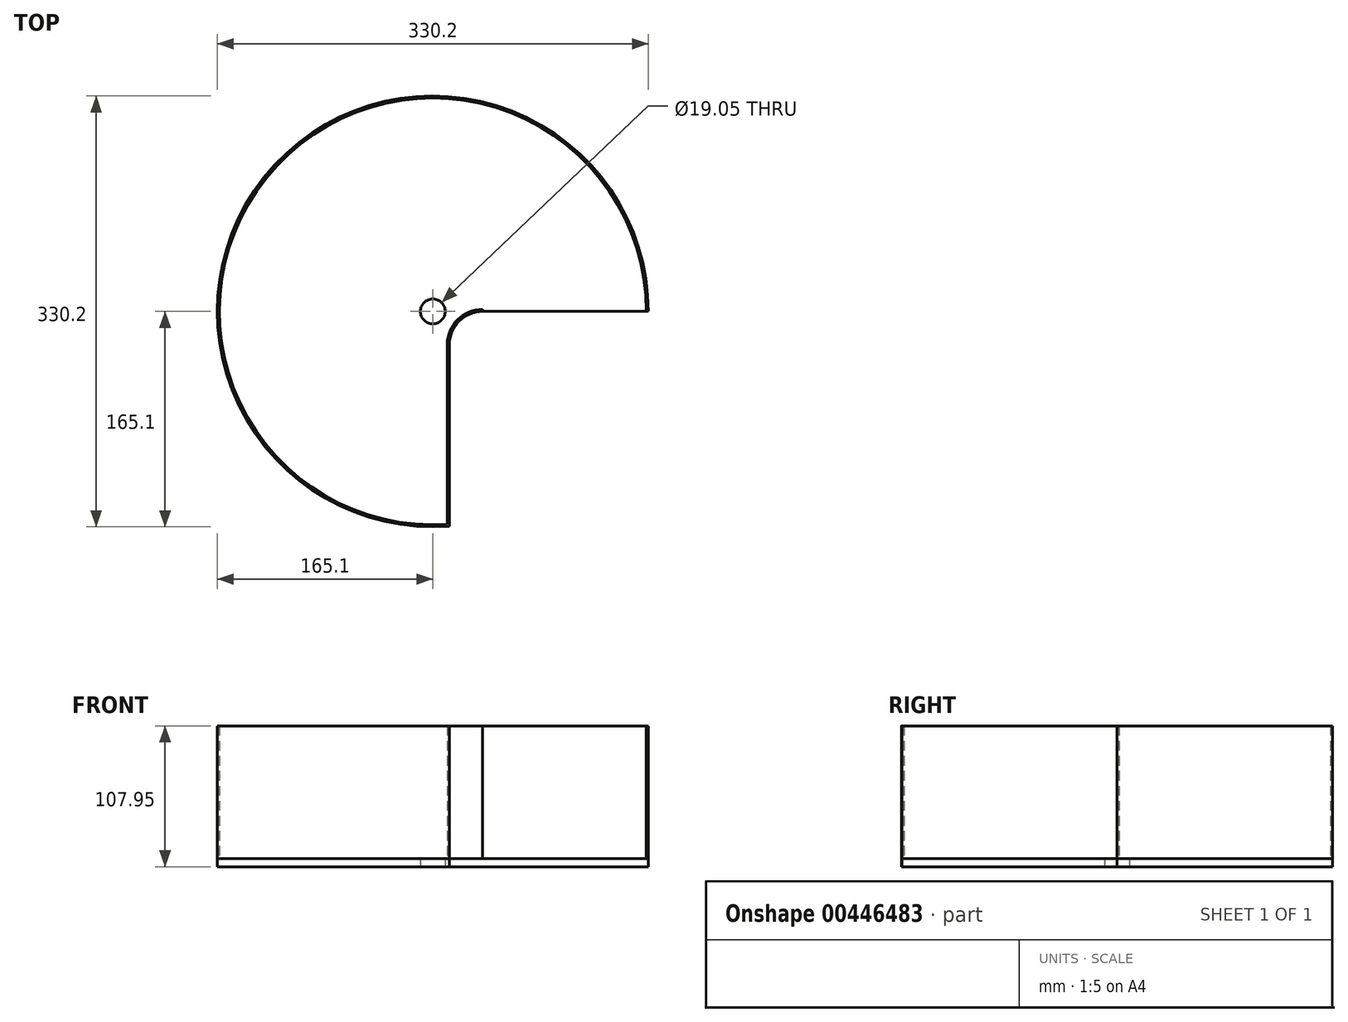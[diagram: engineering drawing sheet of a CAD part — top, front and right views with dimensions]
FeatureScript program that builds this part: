
annotation { "Feature Type Name" : "Feature", "Feature Type Description" : "" }
export const myFeature = defineFeature(function(context is Context, id is Id, definition is map)
    precondition{}
    {
        {
            var Q0;
            Q0=qCreatedBy(makeId("Top.planeOp"),FACE);
            var sketch = newSketch(context, id + "F0", { "sketchPlane" : qUnion([Q0])});
            skArc(sketch, "E0", {"start": v(165.1, 0) * mm, "mid": v(-121.15, 112.16) * mm, "end": v(12.7, -164.61) * mm});
            skLineSegment(sketch, "E1", {"start": v(165.1, 0) * mm, "end": v(38.1, 0) * mm});
            skLineSegment(sketch, "E2", {"start": v(12.7, -25.4) * mm, "end": v(12.7, -164.61) * mm});
            skPoint(sketch, "E3.visualSharp", {"position": v(12.7, 0) * mm});
            skArc(sketch, "E3.filletArc", {"start": v(38.1, 0) * mm, "mid": v(20.14, -7.44) * mm, "end": v(12.7, -25.4) * mm});
            skSolve(sketch);
        }
        {
            var Q0;
            Q0 = qSketchRegion(id + "F0", true);
            extrude(context, id + "F1", {"entities" : qUnion([Q0]), "depth" : 6.35 * mm});
        }
        {
            var Q0;
            Q0=makeQuery(id+"F1.opExtrude","CAP_FACE",FACE,{"disambiguationData":[OSD([sQuery(id+"F0.wireOp",EDGE,"E0"),sQuery(id+"F0.wireOp",EDGE,"E1"),sQuery(id+"F0.wireOp",EDGE,"E2"),sQuery(id+"F0.wireOp",EDGE,"E3.filletArc")])],"isStart":false});
            var sketch = newSketch(context, id + "F2", { "sketchPlane" : qUnion([Q0])});
            skArc(sketch, "E4.0", {"start": v(38.1, 1.59) * mm, "mid": v(19.02, -6.32) * mm, "end": v(11.11, -25.4) * mm});
            skLineSegment(sketch, "E4.1", {"start": v(11.11, -25.4) * mm, "end": v(11.11, -163.13) * mm});
            skArc(sketch, "E4.2", {"start": v(163.51, 0) * mm, "mid": v(-119.49, 111.62) * mm, "end": v(11.11, -163.13) * mm});
            skLineSegment(sketch, "E5", {"start": v(38.1, 1.59) * mm, "end": v(38.1, 0) * mm});
            skLineSegment(sketch, "E6", {"start": v(163.51, 0) * mm, "end": v(165.1, 0) * mm});
            skSolve(sketch);
        }
        {
            var Q0;
            Q0 = qSketchRegion(id + "F2", true);
            var Q1;
            Q1=makeQuery(id+"F2.imprint","IMPRINT",FACE,{"disambiguationData":[TD([[makeQuery(id+"F2.imprint","IMPRINT",EDGE,{"derivedFrom":sQuery(id+"F2.wireOp",EDGE,"E4.0")}),1.0]])]});
            extrude(context, id + "F3", {"entities" : qUnion([Q0, Q1]), "depth" : 101.6 * mm});
        }
        {
            var Q0;
            Q0=makeQuery(id+"F1.opExtrude","CAP_FACE",FACE,{"disambiguationData":[OSD([sQuery(id+"F0.wireOp",EDGE,"E0"),sQuery(id+"F0.wireOp",EDGE,"E1"),sQuery(id+"F0.wireOp",EDGE,"E2"),sQuery(id+"F0.wireOp",EDGE,"E3.filletArc")])],"isStart":false});
            var sketch = newSketch(context, id + "F4", { "sketchPlane" : qUnion([Q0])});
            skPoint(sketch, "E7", {"position": v(0, 0) * mm});
            skSolve(sketch);
        }
        {
            var Q0;
            Q0=sQuery(id+"F4.wireOp",VERTEX,"E7");
            var Q1;
            Q1=makeQuery(id+"F1.opExtrude","SWEPT_BODY",BODY,{"disambiguationData":[OSD([sQuery(id+"F0.wireOp",EDGE,"E0"),sQuery(id+"F0.wireOp",EDGE,"E1"),sQuery(id+"F0.wireOp",EDGE,"E2"),sQuery(id+"F0.wireOp",EDGE,"E3.filletArc")])]});
            hole(context, id + "F5", {"style" : HoleStyle.SIMPLE, "endStyle" : HoleEndStyle.THROUGH, "holeDiameter" : 19.05 * mm, "isTappedThrough" : true, "tappedDepth" : 12.7 * mm, "tapClearance" : 3, "locations" : qUnion([Q0]), "scope" : qUnion([Q1]), "startStyle" : HoleStartStyle.PART});
        }
    });
